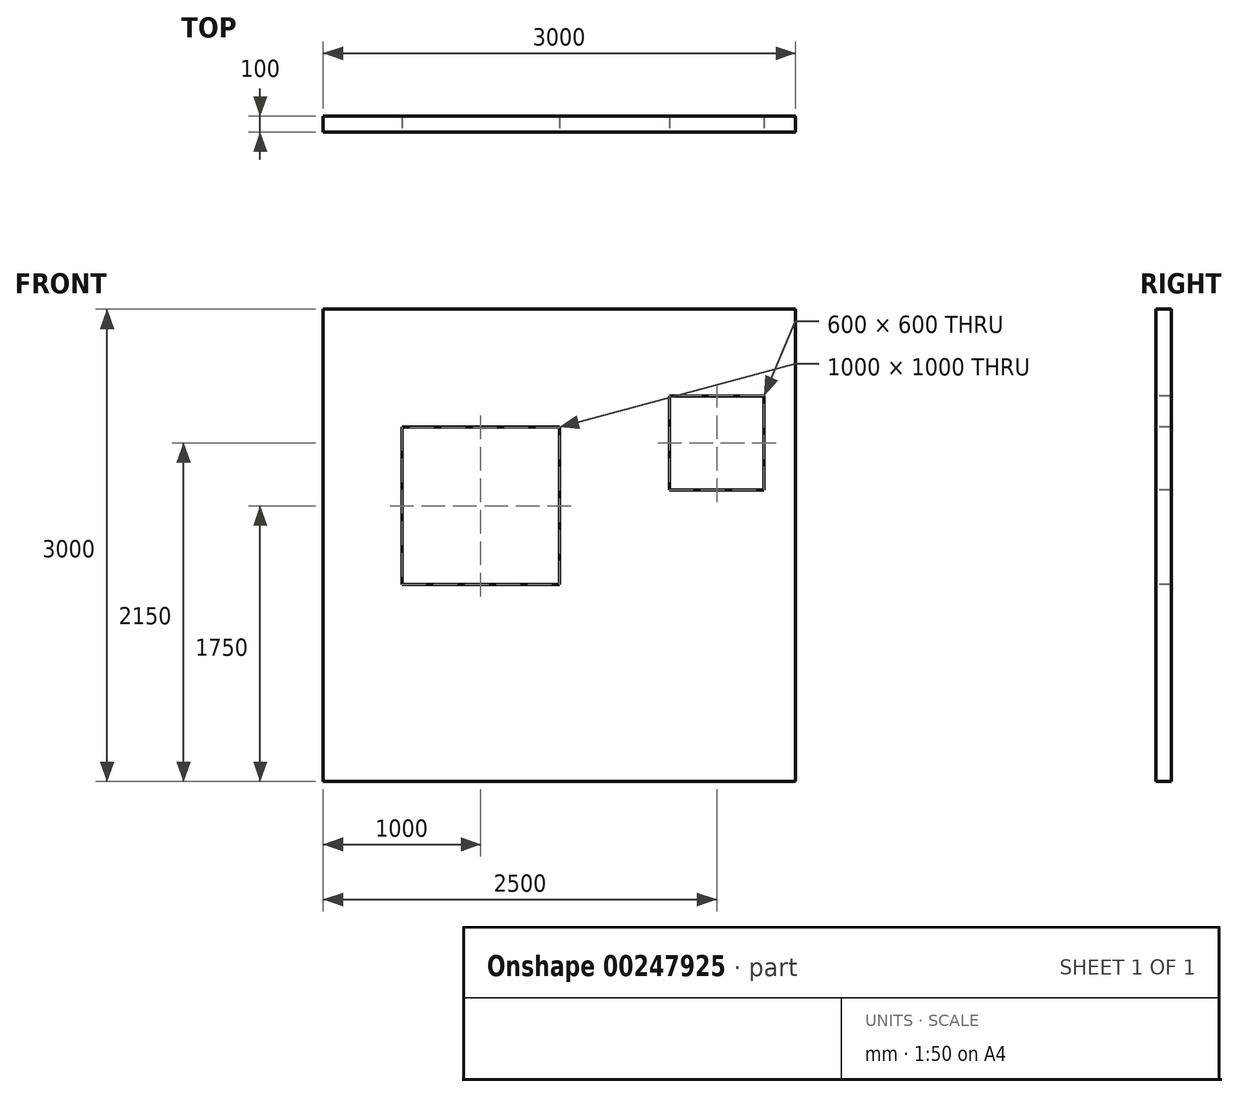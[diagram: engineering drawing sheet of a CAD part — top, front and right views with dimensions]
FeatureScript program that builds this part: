
annotation { "Feature Type Name" : "Feature", "Feature Type Description" : "" }
export const myFeature = defineFeature(function(context is Context, id is Id, definition is map)
    precondition{}
    {
        {
            var Q0;
            Q0=qCreatedBy(makeId("Front.planeOp"),FACE);
            var sketch = newSketch(context, id + "F0", { "sketchPlane" : qUnion([Q0])});
            skLineSegment(sketch, "E0.bottom", {"start": v(1500, 0) * mm, "end": v(-1500, 0) * mm});
            skLineSegment(sketch, "E0.top", {"start": v(1500, 3000) * mm, "end": v(-1500, 3000) * mm});
            skLineSegment(sketch, "E0.left", {"start": v(1500, 0) * mm, "end": v(1500, 3000) * mm});
            skLineSegment(sketch, "E0.right", {"start": v(-1500, 0) * mm, "end": v(-1500, 3000) * mm});
            skPoint(sketch, "E0.middle", {"position": v(0, 1500) * mm});
            skSolve(sketch);
        }
        {
            var Q0;
            Q0=makeQuery(id+"F0.imprint","IMPRINT",FACE,{"disambiguationData":[TD([[makeQuery(id+"F0.imprint","IMPRINT",EDGE,{"derivedFrom":sQuery(id+"F0.wireOp",EDGE,"E0.bottom")}),-1.0]])]});
            extrude(context, id + "F1", {"entities" : qUnion([Q0]), "endBound" : BoundingType.SYMMETRIC, "depth" : 100 * mm});
        }
        {
            var Q0;
            Q0=makeQuery(id+"F1.opExtrude","CAP_FACE",FACE,{"disambiguationData":[OSD([sQuery(id+"F0.wireOp",EDGE,"E0.bottom"),sQuery(id+"F0.wireOp",EDGE,"E0.top"),sQuery(id+"F0.wireOp",EDGE,"E0.left"),sQuery(id+"F0.wireOp",EDGE,"E0.right")])],"isStart":false});
            var sketch = newSketch(context, id + "F2", { "sketchPlane" : qUnion([Q0])});
            skLineSegment(sketch, "E1.bottom", {"start": v(0, 1250) * mm, "end": v(-1000, 1250) * mm});
            skLineSegment(sketch, "E1.top", {"start": v(0, 2250) * mm, "end": v(-1000, 2250) * mm});
            skLineSegment(sketch, "E1.left", {"start": v(0, 1250) * mm, "end": v(0, 2250) * mm});
            skLineSegment(sketch, "E1.right", {"start": v(-1000, 1250) * mm, "end": v(-1000, 2250) * mm});
            skPoint(sketch, "E1.middle", {"position": v(-500, 1750) * mm});
            skLineSegment(sketch, "E2", {"start": v(500, 3000) * mm, "end": v(500, 0) * mm, "construction": true});
            skLineSegment(sketch, "E3", {"start": v(-1500, 3000) * mm, "end": v(500, 3000) * mm, "construction": true});
            skLineSegment(sketch, "E4", {"start": v(1500, 3000) * mm, "end": v(500, 3000) * mm, "construction": true});
            skPoint(sketch, "E5", {"position": v(-500, 3000) * mm});
            skPoint(sketch, "E6", {"position": v(1000, 3000) * mm});
            skLineSegment(sketch, "E7.bottom", {"start": v(1300, 1850) * mm, "end": v(700, 1850) * mm});
            skLineSegment(sketch, "E7.top", {"start": v(1300, 2450) * mm, "end": v(700, 2450) * mm});
            skLineSegment(sketch, "E7.left", {"start": v(1300, 1850) * mm, "end": v(1300, 2450) * mm});
            skLineSegment(sketch, "E7.right", {"start": v(700, 1850) * mm, "end": v(700, 2450) * mm});
            skPoint(sketch, "E7.middle", {"position": v(1000, 2150) * mm});
            skSolve(sketch);
        }
        {
            var Q0;
            Q0=makeQuery(id+"F2.imprint","IMPRINT",FACE,{"disambiguationData":[TD([[makeQuery(id+"F2.imprint","IMPRINT",EDGE,{"derivedFrom":sQuery(id+"F2.wireOp",EDGE,"E1.bottom")}),-1.0]])]});
            var Q1;
            Q1=makeQuery(id+"F2.imprint","IMPRINT",FACE,{"disambiguationData":[TD([[makeQuery(id+"F2.imprint","IMPRINT",EDGE,{"derivedFrom":sQuery(id+"F2.wireOp",EDGE,"E7.bottom")}),-1.0]])]});
            extrude(context, id + "F3", {"entities" : qUnion([Q0, Q1]), "operationType" : NewBodyOperationType.REMOVE, "endBound" : BoundingType.THROUGH_ALL, "oppositeDirection" : true, "depth" : 25 * mm});
        }
    });
